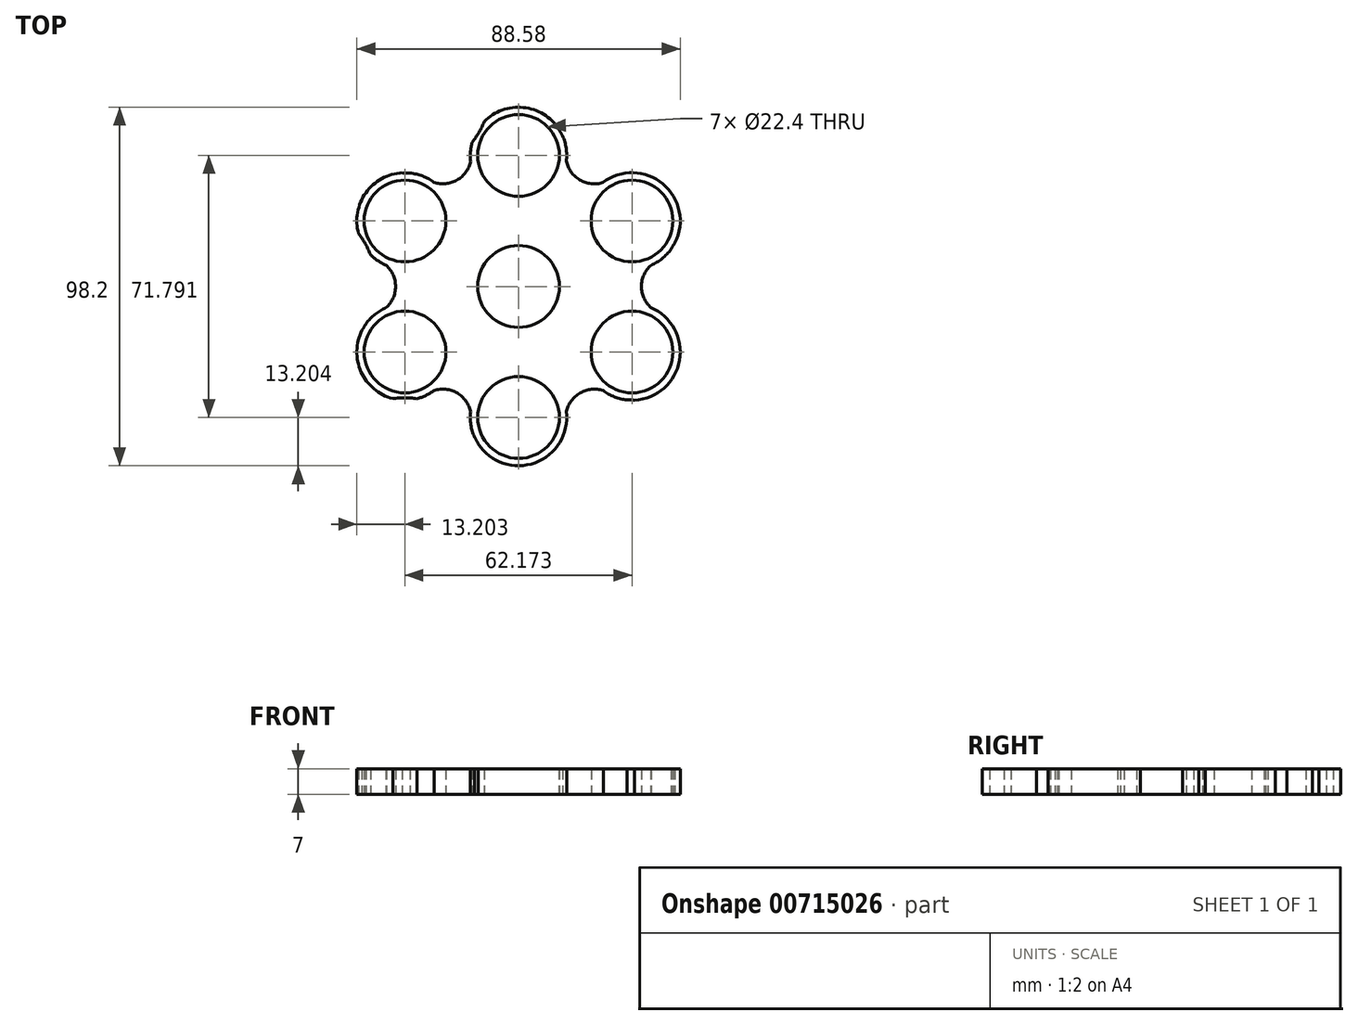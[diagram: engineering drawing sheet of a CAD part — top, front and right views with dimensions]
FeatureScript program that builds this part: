
annotation { "Feature Type Name" : "Feature", "Feature Type Description" : "" }
export const myFeature = defineFeature(function(context is Context, id is Id, definition is map)
    precondition{}
    {
        {
            var Q0;
            Q0=qCreatedBy(makeId("Top.planeOp"),FACE);
            var sketch = newSketch(context, id + "F0", { "sketchPlane" : qUnion([Q0])});
            skCircle(sketch, "E0", {"center": v(0, 35.9) * mm, "radius": 11.2 * mm});
            skArc(sketch, "E1", {"start": v(-12.7, 39.5) * mm, "mid": v(11.4, 29.25) * mm, "end": v(-9.4, 45.17) * mm});
            skPoint(sketch, "E2", {"position": v(0, 54.5) * mm});
            skPoint(sketch, "E3", {"position": v(-48.17, 52.54) * mm});
            skCircle(sketch, "E4.1.0", {"center": v(-31.09, 17.95) * mm, "radius": 11.2 * mm});
            skArc(sketch, "E4.1.1", {"start": v(-40.55, 8.75) * mm, "mid": v(-19.63, 24.5) * mm, "end": v(-43.81, 14.45) * mm});
            skCircle(sketch, "E4.2.0", {"center": v(-31.09, -17.95) * mm, "radius": 11.2 * mm});
            skArc(sketch, "E4.2.1", {"start": v(-27.85, -30.75) * mm, "mid": v(-31.04, -4.75) * mm, "end": v(-34.42, -30.72) * mm});
            skCircle(sketch, "E4.3.0", {"center": v(0, -35.9) * mm, "radius": 11.2 * mm});
            skCircle(sketch, "E4.3.1", {"center": v(0, -35.9) * mm, "radius": 13.2 * mm});
            skCircle(sketch, "E4.4.0", {"center": v(31.09, -17.95) * mm, "radius": 11.2 * mm});
            skCircle(sketch, "E4.4.1", {"center": v(31.09, -17.95) * mm, "radius": 13.2 * mm});
            skCircle(sketch, "E4.5.0", {"center": v(31.09, 17.95) * mm, "radius": 11.2 * mm});
            skCircle(sketch, "E4.5.1", {"center": v(31.09, 17.95) * mm, "radius": 13.2 * mm});
            skPoint(sketch, "E4.center", {"position": v(0, 0) * mm});
            skCircle(sketch, "E5", {"center": v(0, 0) * mm, "radius": 13.2 * mm});
            skCircle(sketch, "E6", {"center": v(0, 0) * mm, "radius": 11.2 * mm});
            skArc(sketch, "E7", {"start": v(-42.87, -12) * mm, "mid": v(-42.3, -11.1) * mm, "end": v(-41.77, -10.2) * mm});
            skArc(sketch, "E8.1.0", {"start": v(-11.05, -43.12) * mm, "mid": v(-11.53, -42.18) * mm, "end": v(-12.06, -41.27) * mm});
            skArc(sketch, "E8.2.0", {"start": v(31.82, -31.13) * mm, "mid": v(30.76, -31.08) * mm, "end": v(29.71, -31.08) * mm});
            skArc(sketch, "E8.3.0", {"start": v(42.87, 12) * mm, "mid": v(42.3, 11.1) * mm, "end": v(41.77, 10.2) * mm});
            skArc(sketch, "E8.4.0", {"start": v(11.05, 43.12) * mm, "mid": v(11.53, 42.18) * mm, "end": v(12.06, 41.27) * mm});
            skArc(sketch, "E8.5.0", {"start": v(-31.82, 31.13) * mm, "mid": v(-30.76, 31.08) * mm, "end": v(-29.71, 31.08) * mm});
            skArc(sketch, "E9", {"start": v(13.1, 34.34) * mm, "mid": v(16.8, 29.18) * mm, "end": v(23.12, 28.47) * mm});
            skArc(sketch, "E10.trimOffspring", {"start": v(-12.7, 39.5) * mm, "mid": v(-10.84, 42.2) * mm, "end": v(-9.4, 45.17) * mm});
            skArc(sketch, "E11.trimOffspring", {"start": v(-40.55, 8.75) * mm, "mid": v(-41.97, 11.72) * mm, "end": v(-43.81, 14.45) * mm});
            skArc(sketch, "E12.trimOffspring", {"start": v(-27.85, -30.75) * mm, "mid": v(-31.13, -30.5) * mm, "end": v(-34.42, -30.72) * mm});
            skArc(sketch, "E13.1.0", {"start": v(-23.19, 28.52) * mm, "mid": v(-16.87, 29.15) * mm, "end": v(-13.1, 34.26) * mm});
            skArc(sketch, "E13.2.0", {"start": v(-36.3, -5.82) * mm, "mid": v(-33.67, -0.03) * mm, "end": v(-36.22, 5.79) * mm});
            skArc(sketch, "E13.3.0", {"start": v(-13.1, -34.34) * mm, "mid": v(-16.8, -29.18) * mm, "end": v(-23.12, -28.47) * mm});
            skArc(sketch, "E13.4.0", {"start": v(23.19, -28.52) * mm, "mid": v(16.87, -29.15) * mm, "end": v(13.1, -34.26) * mm});
            skArc(sketch, "E13.5.0", {"start": v(36.3, 5.82) * mm, "mid": v(33.67, 0.03) * mm, "end": v(36.22, -5.79) * mm});
            skSolve(sketch);
        }
        {
            var Q0;
            Q0=makeQuery(id+"F0.imprint","IMPRINT",FACE,{"disambiguationData":[TD([[makeQuery(id+"F0.imprint","IMPRINT",EDGE,{"derivedFrom":sQuery(id+"F0.wireOp",EDGE,"E4.1.0")}),-1.0]])]});
            var Q1;
            Q1=makeQuery(id+"F0.imprint","IMPRINT",FACE,{"disambiguationData":[TD([[makeQuery(id+"F0.imprint","IMPRINT",EDGE,{"derivedFrom":sQuery(id+"F0.wireOp",EDGE,"E0")}),-1.0]])]});
            var Q2;
            Q2=makeQuery(id+"F0.imprint","IMPRINT",FACE,{"disambiguationData":[TD([[makeQuery(id+"F0.imprint","IMPRINT",EDGE,{"derivedFrom":sQuery(id+"F0.wireOp",EDGE,"E4.5.0")}),-1.0]])]});
            var Q3;
            Q3=makeQuery(id+"F0.imprint","IMPRINT",FACE,{"disambiguationData":[TD([[makeQuery(id+"F0.imprint","IMPRINT",EDGE,{"derivedFrom":sQuery(id+"F0.wireOp",EDGE,"E1")}),-1.0]])]});
            var Q4;
            Q4=makeQuery(id+"F0.imprint","IMPRINT",FACE,{"disambiguationData":[TD([[makeQuery(id+"F0.imprint","IMPRINT",EDGE,{"derivedFrom":sQuery(id+"F0.wireOp",EDGE,"E4.4.0")}),-1.0]])]});
            var Q5;
            Q5=makeQuery(id+"F0.imprint","IMPRINT",FACE,{"disambiguationData":[TD([[makeQuery(id+"F0.imprint","IMPRINT",EDGE,{"derivedFrom":sQuery(id+"F0.wireOp",EDGE,"E4.3.0")}),-1.0]])]});
            var Q6;
            Q6=makeQuery(id+"F0.imprint","IMPRINT",FACE,{"disambiguationData":[TD([[makeQuery(id+"F0.imprint","IMPRINT",EDGE,{"derivedFrom":sQuery(id+"F0.wireOp",EDGE,"E4.2.0")}),-1.0]])]});
            var Q7;
            Q7=makeQuery(id+"F0.imprint","IMPRINT",FACE,{"disambiguationData":[TD([[makeQuery(id+"F0.imprint","IMPRINT",EDGE,{"derivedFrom":sQuery(id+"F0.wireOp",EDGE,"E5")}),1.0]])]});
            extrude(context, id + "F1", {"entities" : qUnion([Q0, Q1, Q2, Q3, Q4, Q5, Q6, Q7]), "depth" : 7 * mm, "offsetDistance" : 25 * mm});
        }
    });
